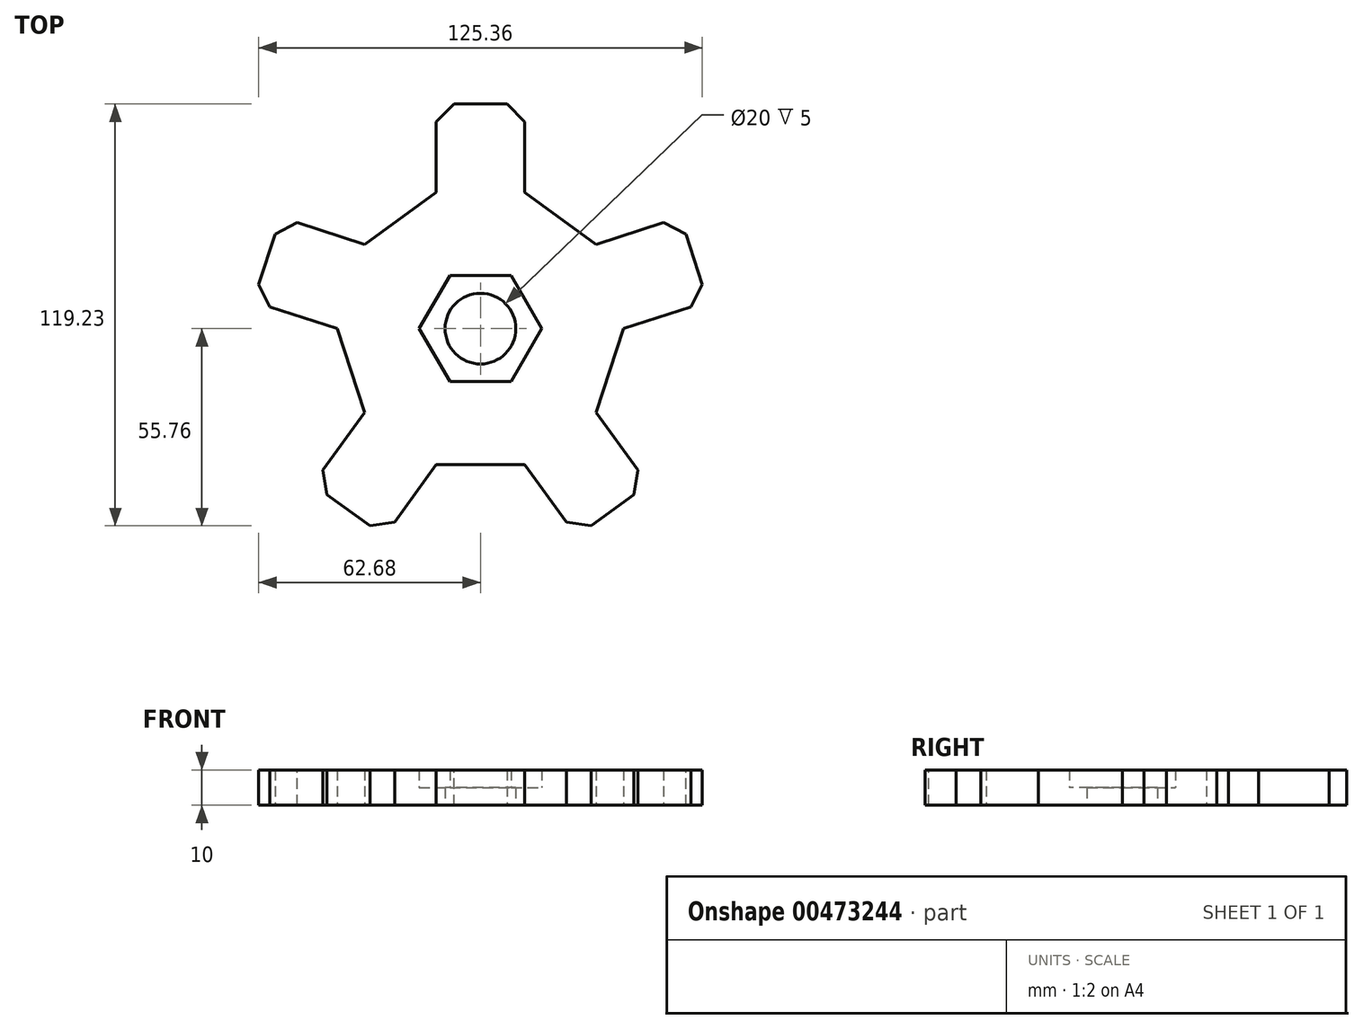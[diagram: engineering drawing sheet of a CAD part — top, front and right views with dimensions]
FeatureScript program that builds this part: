
annotation { "Feature Type Name" : "Feature", "Feature Type Description" : "" }
export const myFeature = defineFeature(function(context is Context, id is Id, definition is map)
    precondition{}
    {
        {
            var Q0;
            Q0=qCreatedBy(makeId("Top.planeOp"),FACE);
            var sketch = newSketch(context, id + "F0", { "sketchPlane" : qUnion([Q0])});
            skCircle(sketch, "E0.cCircle", {"center": v(0, 0) * mm, "radius": 38.47 * mm, "construction": true});
            skLineSegment(sketch, "E0.0", {"start": v(-12.5, 38.47) * mm, "end": v(12.5, 38.47) * mm});
            skLineSegment(sketch, "E0.1", {"start": v(12.5, 38.47) * mm, "end": v(32.73, 23.78) * mm});
            skLineSegment(sketch, "E0.2", {"start": v(32.73, 23.78) * mm, "end": v(40.45, 0) * mm});
            skLineSegment(sketch, "E0.3", {"start": v(40.45, 0) * mm, "end": v(32.73, -23.78) * mm});
            skLineSegment(sketch, "E0.4", {"start": v(32.73, -23.78) * mm, "end": v(12.5, -38.47) * mm});
            skLineSegment(sketch, "E0.5", {"start": v(12.5, -38.47) * mm, "end": v(-12.5, -38.47) * mm});
            skLineSegment(sketch, "E0.6", {"start": v(-12.5, -38.47) * mm, "end": v(-32.73, -23.78) * mm});
            skLineSegment(sketch, "E0.7", {"start": v(-32.73, -23.78) * mm, "end": v(-40.45, 0) * mm});
            skLineSegment(sketch, "E0.8", {"start": v(-40.45, 0) * mm, "end": v(-32.73, 23.78) * mm});
            skLineSegment(sketch, "E0.9", {"start": v(-32.73, 23.78) * mm, "end": v(-12.5, 38.47) * mm});
            skPoint(sketch, "E0.0.midPoint", {"position": v(0, 38.47) * mm});
            skCircle(sketch, "E1.cCircle", {"center": v(0, 0) * mm, "radius": 15 * mm, "construction": true});
            skPoint(sketch, "E1.cCircle.perimeterSnap0", {"position": v(-36.59, 11.89) * mm});
            skLineSegment(sketch, "E1.0", {"start": v(-8.66, 15) * mm, "end": v(8.66, 15) * mm});
            skLineSegment(sketch, "E1.1", {"start": v(8.66, 15) * mm, "end": v(17.32, 0) * mm});
            skLineSegment(sketch, "E1.2", {"start": v(17.32, 0) * mm, "end": v(8.66, -15) * mm});
            skLineSegment(sketch, "E1.3", {"start": v(8.66, -15) * mm, "end": v(-8.66, -15) * mm});
            skLineSegment(sketch, "E1.4", {"start": v(-8.66, -15) * mm, "end": v(-17.32, 0) * mm});
            skLineSegment(sketch, "E1.5", {"start": v(-17.32, 0) * mm, "end": v(-8.66, 15) * mm});
            skPoint(sketch, "E1.0.midPoint", {"position": v(0, 15) * mm});
            skPoint(sketch, "E1.0.midPoint.positionSnap0", {"position": v(-36.59, 11.89) * mm});
            skCircle(sketch, "E2", {"center": v(0, 0) * mm, "radius": 10 * mm});
            skSolve(sketch);
        }
        {
            var Q0;
            Q0 = qSketchRegion(id + "F0", true);
            extrude(context, id + "F1", {"entities" : qUnion([Q0]), "depth" : 10 * mm});
        }
        {
            var Q0;
            Q0=makeQuery(id+"F1.opExtrude","SWEPT_FACE",FACE,{"disambiguationData":[OSD([sQuery(id+"F0.wireOp",EDGE,"E0.2")])]});
            extrude(context, id + "F2", {"entities" : qUnion([Q0]), "operationType" : NewBodyOperationType.ADD, "depth" : 25 * mm});
        }
        {
            var Q0;
            Q0=makeQuery(id+"F1.opExtrude","SWEPT_FACE",FACE,{"disambiguationData":[OSD([sQuery(id+"F0.wireOp",EDGE,"E0.0")])]});
            extrude(context, id + "F3", {"entities" : qUnion([Q0]), "operationType" : NewBodyOperationType.ADD, "depth" : 25 * mm});
        }
        {
            var Q0;
            Q0=makeQuery(id+"F1.opExtrude","SWEPT_FACE",FACE,{"disambiguationData":[OSD([sQuery(id+"F0.wireOp",EDGE,"E0.4")])]});
            extrude(context, id + "F4", {"entities" : qUnion([Q0]), "operationType" : NewBodyOperationType.ADD, "depth" : 25 * mm});
        }
        {
            var Q0;
            Q0=makeQuery(id+"F1.opExtrude","SWEPT_FACE",FACE,{"disambiguationData":[OSD([sQuery(id+"F0.wireOp",EDGE,"E0.8")])]});
            extrude(context, id + "F5", {"entities" : qUnion([Q0]), "operationType" : NewBodyOperationType.ADD, "depth" : 25 * mm});
        }
        {
            var Q0;
            Q0=makeQuery(id+"F1.opExtrude","SWEPT_FACE",FACE,{"disambiguationData":[OSD([sQuery(id+"F0.wireOp",EDGE,"E0.6")])]});
            extrude(context, id + "F6", {"entities" : qUnion([Q0]), "operationType" : NewBodyOperationType.ADD, "depth" : 25 * mm});
        }
        {
            var Q0;
            Q0=makeQuery(id+"F5.opExtrude","CAP_EDGE",EDGE,{"disambiguationData":[OSD([sQuery(id+"F0.wireOp",EDGE,"E0.7"),sQuery(id+"F0.wireOp",EDGE,"E0.8")])],"isStart":false});
            var Q1;
            Q1=makeQuery(id+"F5.opExtrude","CAP_EDGE",EDGE,{"disambiguationData":[OSD([sQuery(id+"F0.wireOp",EDGE,"E0.8"),sQuery(id+"F0.wireOp",EDGE,"E0.9")])],"isStart":false});
            var Q2;
            Q2=makeQuery(id+"F3.opExtrude","CAP_EDGE",EDGE,{"disambiguationData":[OSD([sQuery(id+"F0.wireOp",EDGE,"E0.0"),sQuery(id+"F0.wireOp",EDGE,"E0.9")])],"isStart":false});
            var Q3;
            Q3=makeQuery(id+"F6.opExtrude","CAP_EDGE",EDGE,{"disambiguationData":[OSD([sQuery(id+"F0.wireOp",EDGE,"E0.6"),sQuery(id+"F0.wireOp",EDGE,"E0.7")])],"isStart":false});
            var Q4;
            Q4=makeQuery(id+"F6.opExtrude","CAP_EDGE",EDGE,{"disambiguationData":[OSD([sQuery(id+"F0.wireOp",EDGE,"E0.5"),sQuery(id+"F0.wireOp",EDGE,"E0.6")])],"isStart":false});
            var Q5;
            Q5=makeQuery(id+"F4.opExtrude","CAP_EDGE",EDGE,{"disambiguationData":[OSD([sQuery(id+"F0.wireOp",EDGE,"E0.4"),sQuery(id+"F0.wireOp",EDGE,"E0.5")])],"isStart":false});
            var Q6;
            Q6=makeQuery(id+"F2.opExtrude","CAP_EDGE",EDGE,{"disambiguationData":[OSD([sQuery(id+"F0.wireOp",EDGE,"E0.2"),sQuery(id+"F0.wireOp",EDGE,"E0.3")])],"isStart":false});
            var Q7;
            Q7=makeQuery(id+"F3.opExtrude","CAP_EDGE",EDGE,{"disambiguationData":[OSD([sQuery(id+"F0.wireOp",EDGE,"E0.0"),sQuery(id+"F0.wireOp",EDGE,"E0.1")])],"isStart":false});
            var Q8;
            Q8=makeQuery(id+"F2.opExtrude","CAP_EDGE",EDGE,{"disambiguationData":[OSD([sQuery(id+"F0.wireOp",EDGE,"E0.1"),sQuery(id+"F0.wireOp",EDGE,"E0.2")])],"isStart":false});
            var Q9;
            Q9=makeQuery(id+"F4.opExtrude","CAP_EDGE",EDGE,{"disambiguationData":[OSD([sQuery(id+"F0.wireOp",EDGE,"E0.3"),sQuery(id+"F0.wireOp",EDGE,"E0.4")])],"isStart":false});
            chamfer(context, id + "F7", {"entities" : qUnion([Q0, Q1, Q2, Q3, Q4, Q5, Q6, Q7, Q8, Q9]), "width" : 5 * mm, "tangentPropagation" : true});
        }
        {
            var Q0;
            Q0=makeQuery(id+"F0.imprint","IMPRINT",FACE,{"disambiguationData":[TD([[makeQuery(id+"F0.imprint","IMPRINT",EDGE,{"derivedFrom":sQuery(id+"F0.wireOp",EDGE,"E1.0")}),-1.0]])]});
            extrude(context, id + "F8", {"entities" : qUnion([Q0]), "operationType" : NewBodyOperationType.ADD, "depth" : 5 * mm});
        }
    });
